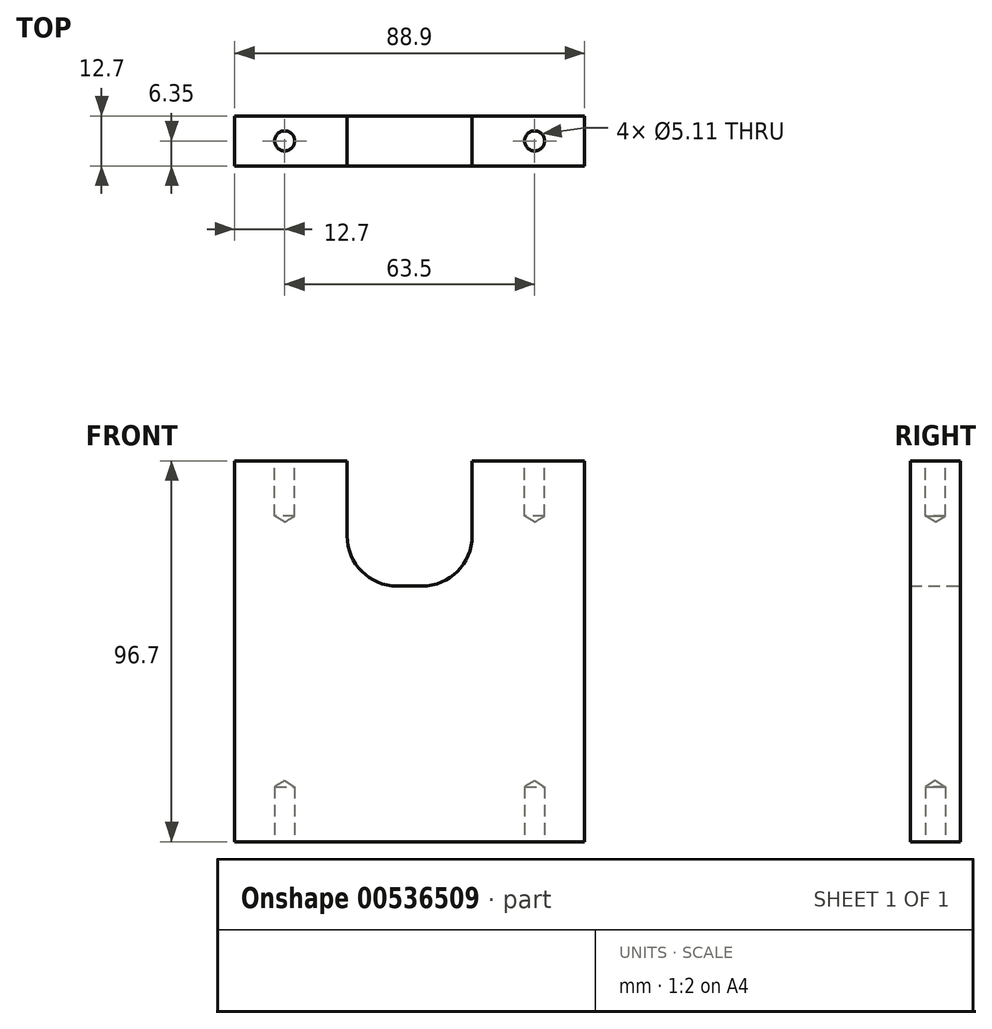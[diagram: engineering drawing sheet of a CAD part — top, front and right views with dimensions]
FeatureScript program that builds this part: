
annotation { "Feature Type Name" : "Feature", "Feature Type Description" : "" }
export const myFeature = defineFeature(function(context is Context, id is Id, definition is map)
    precondition{}
    {
        {
            var Q0;
            Q0=qCreatedBy(makeId("Top.planeOp"),FACE);
            var sketch = newSketch(context, id + "F0", { "sketchPlane" : qUnion([Q0])});
            skLineSegment(sketch, "E0.bottom", {"start": v(0, 0) * mm, "end": v(-88.9, 0) * mm});
            skLineSegment(sketch, "E0.top", {"start": v(0, 12.7) * mm, "end": v(-88.9, 12.7) * mm});
            skLineSegment(sketch, "E0.left", {"start": v(0, 0) * mm, "end": v(0, 12.7) * mm});
            skLineSegment(sketch, "E0.right", {"start": v(-88.9, 0) * mm, "end": v(-88.9, 12.7) * mm});
            skSolve(sketch);
        }
        {
            var Q0;
            Q0=makeQuery(id+"F0.imprint","IMPRINT",FACE,{"disambiguationData":[TD([[makeQuery(id+"F0.imprint","IMPRINT",EDGE,{"derivedFrom":sQuery(id+"F0.wireOp",EDGE,"E0.bottom")}),-1.0]])]});
            extrude(context, id + "F1", {"entities" : qUnion([Q0]), "depth" : 96.7 * mm, "offsetDistance" : 25.4 * mm});
        }
        {
            var Q0;
            Q0=makeQuery(id+"F1.opExtrude","CAP_FACE",FACE,{"disambiguationData":[OSD([sQuery(id+"F0.wireOp",EDGE,"E0.bottom"),sQuery(id+"F0.wireOp",EDGE,"E0.top"),sQuery(id+"F0.wireOp",EDGE,"E0.left"),sQuery(id+"F0.wireOp",EDGE,"E0.right")])],"isStart":false});
            var sketch = newSketch(context, id + "F2", { "sketchPlane" : qUnion([Q0])});
            skLineSegment(sketch, "E1", {"start": v(-88.9, 6.35) * mm, "end": v(-76.2, 6.35) * mm, "construction": true});
            skLineSegment(sketch, "E2", {"start": v(-76.2, 6.35) * mm, "end": v(-12.7, 6.35) * mm, "construction": true});
            skLineSegment(sketch, "E3", {"start": v(-12.7, 6.35) * mm, "end": v(0, 6.35) * mm, "construction": true});
            skLineSegment(sketch, "E4", {"start": v(-44.45, 6.35) * mm, "end": v(-44.45, 12.7) * mm, "construction": true});
            skSolve(sketch);
        }
        {
            var Q0;
            Q0=sQuery(id+"F2.wireOp",VERTEX,"E2.start");
            var Q1;
            Q1=sQuery(id+"F2.wireOp",VERTEX,"E3.start");
            var Q2;
            Q2=makeQuery(id+"F1.opExtrude","SWEPT_BODY",BODY,{"disambiguationData":[OSD([sQuery(id+"F0.wireOp",EDGE,"E0.bottom"),sQuery(id+"F0.wireOp",EDGE,"E0.top"),sQuery(id+"F0.wireOp",EDGE,"E0.left"),sQuery(id+"F0.wireOp",EDGE,"E0.right")])]});
            hole(context, id + "F3", {"style" : HoleStyle.SIMPLE, "endStyle" : HoleEndStyle.BLIND, "standardTappedOrClearance" : lookupTablePath({ "standard" : "ANSI", "engagement" : "75%", "pitch" : "20 tpi", "size" : "1/4", "type" : "Tapped" }), "standardBlindInLast" : lookupTablePath({ "standard" : "ANSI", "engagement" : "75%", "pitch" : "20 tpi", "size" : "1/4", "type" : "Tapped" }), "holeDiameter" : 5.1 * mm, "majorDiameter" : 6.35 * mm, "showTappedDepth" : true, "holeDepth" : 13.97 * mm, "tappedDepth" : 12.7 * mm, "tapClearance" : 1, "startFromSketch" : true, "locations" : qUnion([Q0, Q1]), "scope" : qUnion([Q2])});
        }
        {
            var Q0;
            Q0=makeQuery(id+"F1.opExtrude","CAP_FACE",FACE,{"disambiguationData":[OSD([sQuery(id+"F0.wireOp",EDGE,"E0.bottom"),sQuery(id+"F0.wireOp",EDGE,"E0.top"),sQuery(id+"F0.wireOp",EDGE,"E0.left"),sQuery(id+"F0.wireOp",EDGE,"E0.right")])],"isStart":true});
            var sketch = newSketch(context, id + "F4", { "sketchPlane" : qUnion([Q0])});
            skLineSegment(sketch, "E5", {"start": v(-88.9, -6.35) * mm, "end": v(-76.2, -6.35) * mm, "construction": true});
            skLineSegment(sketch, "E6", {"start": v(-76.2, -6.35) * mm, "end": v(-12.7, -6.35) * mm, "construction": true});
            skLineSegment(sketch, "E7", {"start": v(-12.7, -6.35) * mm, "end": v(0, -6.35) * mm, "construction": true});
            skLineSegment(sketch, "E8", {"start": v(-44.45, -6.35) * mm, "end": v(-44.45, 0) * mm, "construction": true});
            skSolve(sketch);
        }
        {
            var Q0;
            Q0=sQuery(id+"F4.wireOp",VERTEX,"E6.start");
            var Q1;
            Q1=sQuery(id+"F4.wireOp",VERTEX,"E7.start");
            var Q2;
            Q2=makeQuery(id+"F1.opExtrude","SWEPT_BODY",BODY,{"disambiguationData":[OSD([sQuery(id+"F0.wireOp",EDGE,"E0.bottom"),sQuery(id+"F0.wireOp",EDGE,"E0.top"),sQuery(id+"F0.wireOp",EDGE,"E0.left"),sQuery(id+"F0.wireOp",EDGE,"E0.right")])]});
            hole(context, id + "F5", {"style" : HoleStyle.SIMPLE, "endStyle" : HoleEndStyle.BLIND, "standardTappedOrClearance" : lookupTablePath({ "standard" : "ANSI", "engagement" : "75%", "pitch" : "20 tpi", "size" : "1/4", "type" : "Tapped" }), "standardBlindInLast" : lookupTablePath({ "standard" : "ANSI", "engagement" : "75%", "pitch" : "20 tpi", "size" : "1/4", "type" : "Tapped" }), "holeDiameter" : 5.1 * mm, "majorDiameter" : 6.35 * mm, "showTappedDepth" : true, "holeDepth" : 13.97 * mm, "tappedDepth" : 12.7 * mm, "tapClearance" : 1, "startFromSketch" : true, "locations" : qUnion([Q0, Q1]), "scope" : qUnion([Q2])});
        }
        {
            var Q0;
            Q0=makeQuery(id+"F1.opExtrude","SWEPT_FACE",FACE,{"disambiguationData":[OSD([sQuery(id+"F0.wireOp",EDGE,"E0.top")])]});
            var sketch = newSketch(context, id + "F6", { "sketchPlane" : qUnion([Q0])});
            skLineSegment(sketch, "E9.bottom", {"start": v(60.32, 96.7) * mm, "end": v(28.58, 96.7) * mm});
            skLineSegment(sketch, "E9.top", {"start": v(47.62, 64.95) * mm, "end": v(41.28, 64.95) * mm});
            skLineSegment(sketch, "E9.left", {"start": v(60.33, 96.7) * mm, "end": v(60.33, 77.65) * mm});
            skLineSegment(sketch, "E9.right", {"start": v(28.58, 96.7) * mm, "end": v(28.58, 77.65) * mm});
            skLineSegment(sketch, "E10", {"start": v(44.45, 64.95) * mm, "end": v(44.45, 0) * mm, "construction": true});
            skPoint(sketch, "E11.visualSharp", {"position": v(60.32, 64.95) * mm});
            skArc(sketch, "E11.filletArc", {"start": v(47.62, 64.95) * mm, "mid": v(56.6, 68.67) * mm, "end": v(60.32, 77.65) * mm});
            skPoint(sketch, "E12.visualSharp", {"position": v(28.57, 64.95) * mm});
            skArc(sketch, "E12.filletArc", {"start": v(28.58, 77.65) * mm, "mid": v(32.3, 68.67) * mm, "end": v(41.28, 64.95) * mm});
            skSolve(sketch);
        }
        {
            var Q0;
            Q0 = qSketchRegion(id + "F6", true);
            extrude(context, id + "F7", {"entities" : qUnion([Q0]), "operationType" : NewBodyOperationType.REMOVE, "oppositeDirection" : true, "depth" : 25.4 * mm, "offsetDistance" : 25.4 * mm});
        }
    });
